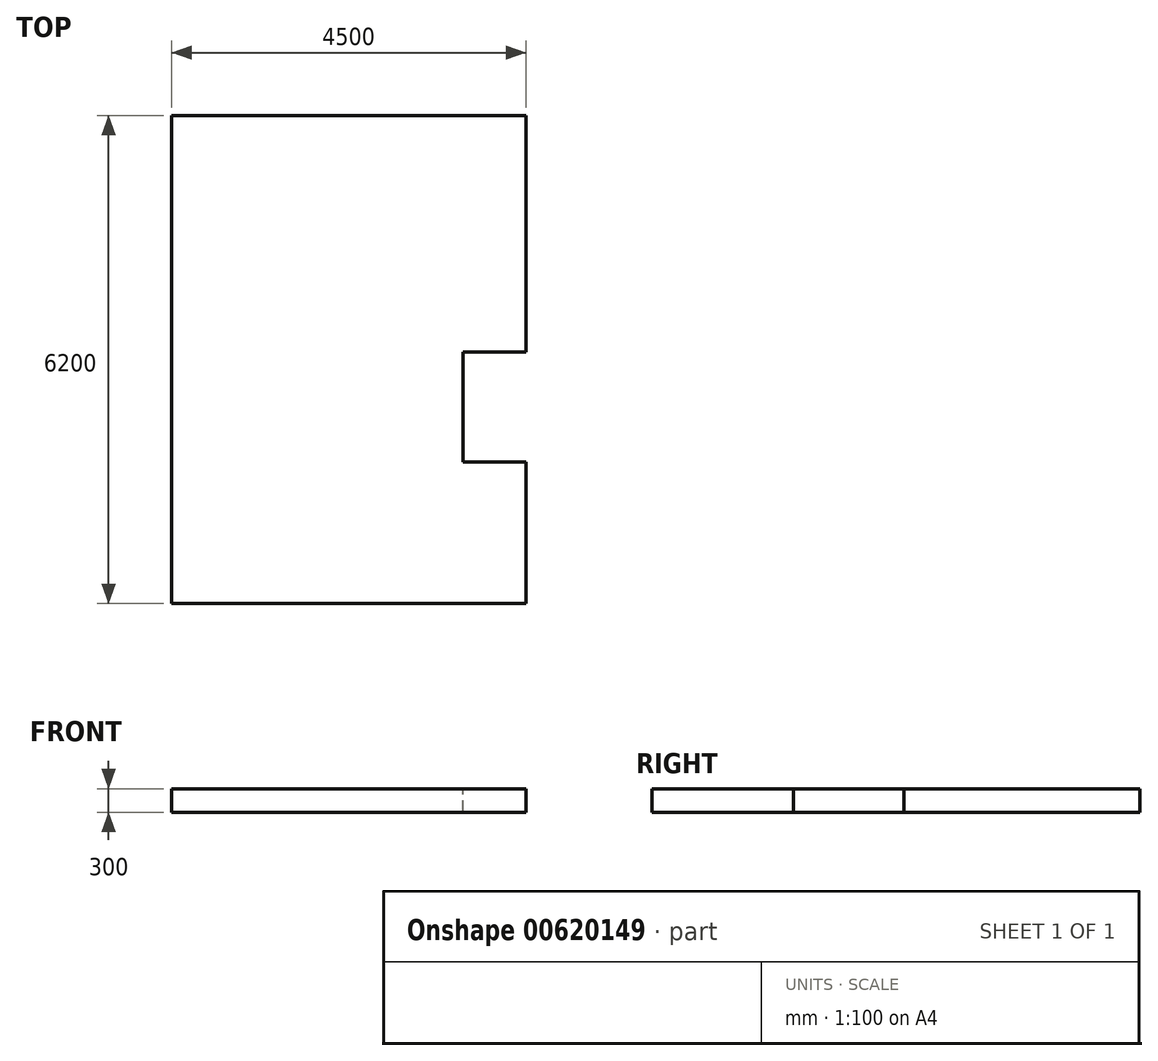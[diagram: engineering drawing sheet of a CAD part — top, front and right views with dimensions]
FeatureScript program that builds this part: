
annotation { "Feature Type Name" : "Feature", "Feature Type Description" : "" }
export const myFeature = defineFeature(function(context is Context, id is Id, definition is map)
    precondition{}
    {
        {
            var Q0;
            Q0=qCreatedBy(makeId("Top.planeOp"),FACE);
            var sketch = newSketch(context, id + "F0", { "sketchPlane" : qUnion([Q0])});
            skLineSegment(sketch, "E0.bottom", {"start": v(-2375, -3100) * mm, "end": v(2125, -3100) * mm});
            skLineSegment(sketch, "E0.top", {"start": v(-2375, 3100) * mm, "end": v(2125, 3100) * mm});
            skLineSegment(sketch, "E0.left", {"start": v(-2375, -3100) * mm, "end": v(-2375, 3100) * mm});
            skLineSegment(sketch, "E0.right", {"start": v(2125, -3100) * mm, "end": v(2125, 3100) * mm});
            skSolve(sketch);
        }
        {
            var Q0;
            Q0 = qSketchRegion(id + "F0", true);
            extrude(context, id + "F1", {"entities" : qUnion([Q0]), "endBound" : BoundingType.SYMMETRIC, "depth" : 300 * mm, "offsetDistance" : 25 * mm});
        }
        {
            var Q0;
            Q0=qCreatedBy(makeId("Top.planeOp"),FACE);
            var sketch = newSketch(context, id + "F2", { "sketchPlane" : qUnion([Q0])});
            skLineSegment(sketch, "E1.bottom", {"start": v(1325, 100) * mm, "end": v(2125, 100) * mm});
            skLineSegment(sketch, "E1.top", {"start": v(1325, -1300) * mm, "end": v(2125, -1300) * mm});
            skLineSegment(sketch, "E1.left", {"start": v(1325, 100) * mm, "end": v(1325, -1300) * mm});
            skLineSegment(sketch, "E1.right", {"start": v(2125, 100) * mm, "end": v(2125, -1300) * mm});
            skSolve(sketch);
        }
        {
            var Q0;
            Q0 = qSketchRegion(id + "F2", true);
            extrude(context, id + "F3", {"entities" : qUnion([Q0]), "operationType" : NewBodyOperationType.REMOVE, "endBound" : BoundingType.SYMMETRIC, "oppositeDirection" : true, "depth" : 300 * mm, "offsetDistance" : 25 * mm});
        }
    });
